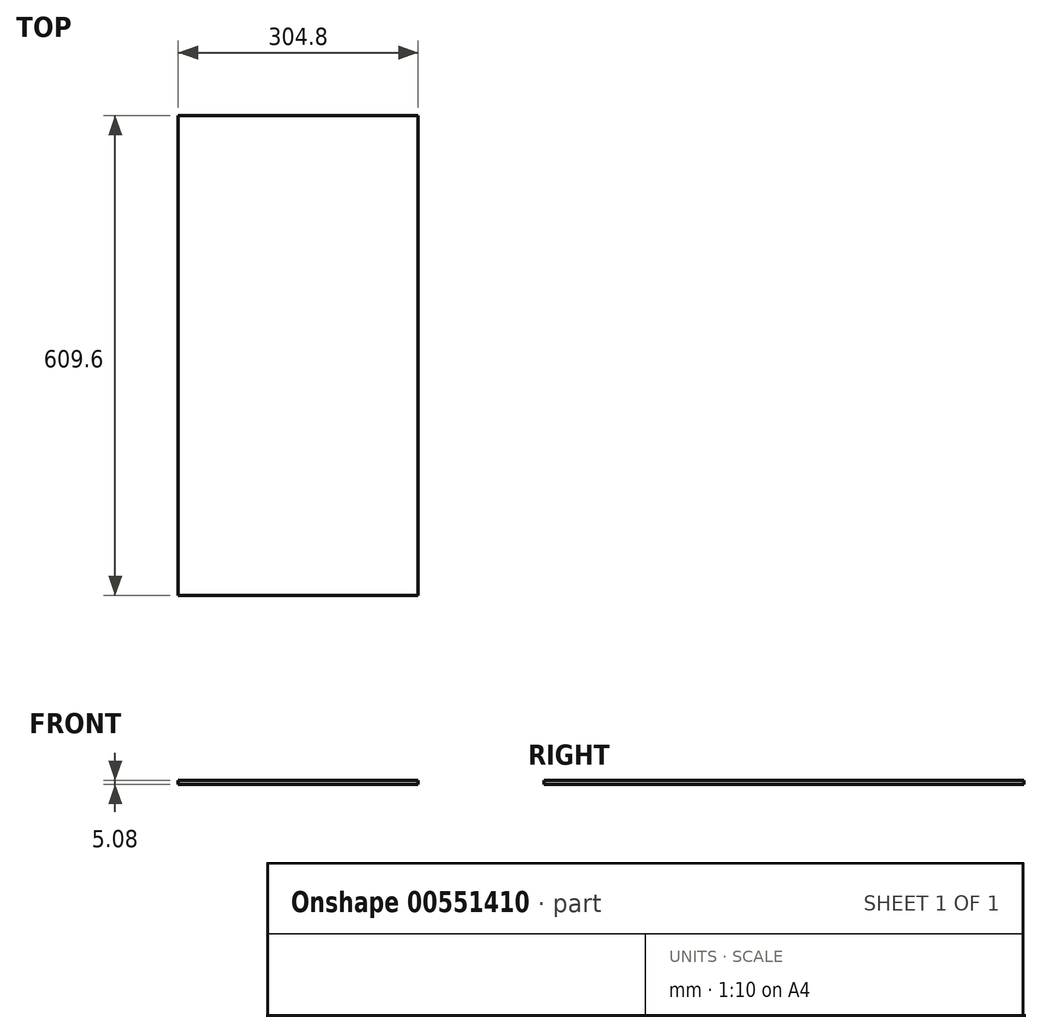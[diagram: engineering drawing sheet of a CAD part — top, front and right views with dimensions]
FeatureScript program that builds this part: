
annotation { "Feature Type Name" : "Feature", "Feature Type Description" : "" }
export const myFeature = defineFeature(function(context is Context, id is Id, definition is map)
    precondition{}
    {
        {
            var Q0;
            Q0=qCreatedBy(makeId("Top.planeOp"),FACE);
            var sketch = newSketch(context, id + "F0", { "sketchPlane" : qUnion([Q0])});
            skLineSegment(sketch, "E0.bottom", {"start": v(-303.74, 305.74) * mm, "end": v(1.06, 305.74) * mm});
            skLineSegment(sketch, "E0.top", {"start": v(-303.74, -303.86) * mm, "end": v(1.06, -303.86) * mm});
            skLineSegment(sketch, "E0.left", {"start": v(-303.74, 305.74) * mm, "end": v(-303.74, -303.86) * mm});
            skLineSegment(sketch, "E0.right", {"start": v(1.06, 305.74) * mm, "end": v(1.06, -303.86) * mm});
            skPoint(sketch, "E1", {"position": v(1.06, 0.94) * mm});
            skPoint(sketch, "E2", {"position": v(-303.74, 0.94) * mm});
            skLineSegment(sketch, "E3", {"start": v(-303.74, 0.94) * mm, "end": v(1.06, 0.94) * mm, "construction": true});
            skLineSegment(sketch, "E4", {"start": v(-151.34, 0.94) * mm, "end": v(-151.34, -303.86) * mm, "construction": true});
            skLineSegment(sketch, "E5", {"start": v(-151.34, -303.86) * mm, "end": v(-151.34, 0.94) * mm, "construction": true});
            skLineSegment(sketch, "E6", {"start": v(-151.34, 0.94) * mm, "end": v(-151.34, 305.74) * mm, "construction": true});
            skSolve(sketch);
        }
        {
            var Q0;
            Q0=qSketchRegion(id+"F0",true);
            extrude(context, id + "F1", {"entities" : qUnion([Q0]), "depth" : 5.08 * mm, "offsetDistance" : 25.4 * mm});
        }
    });
